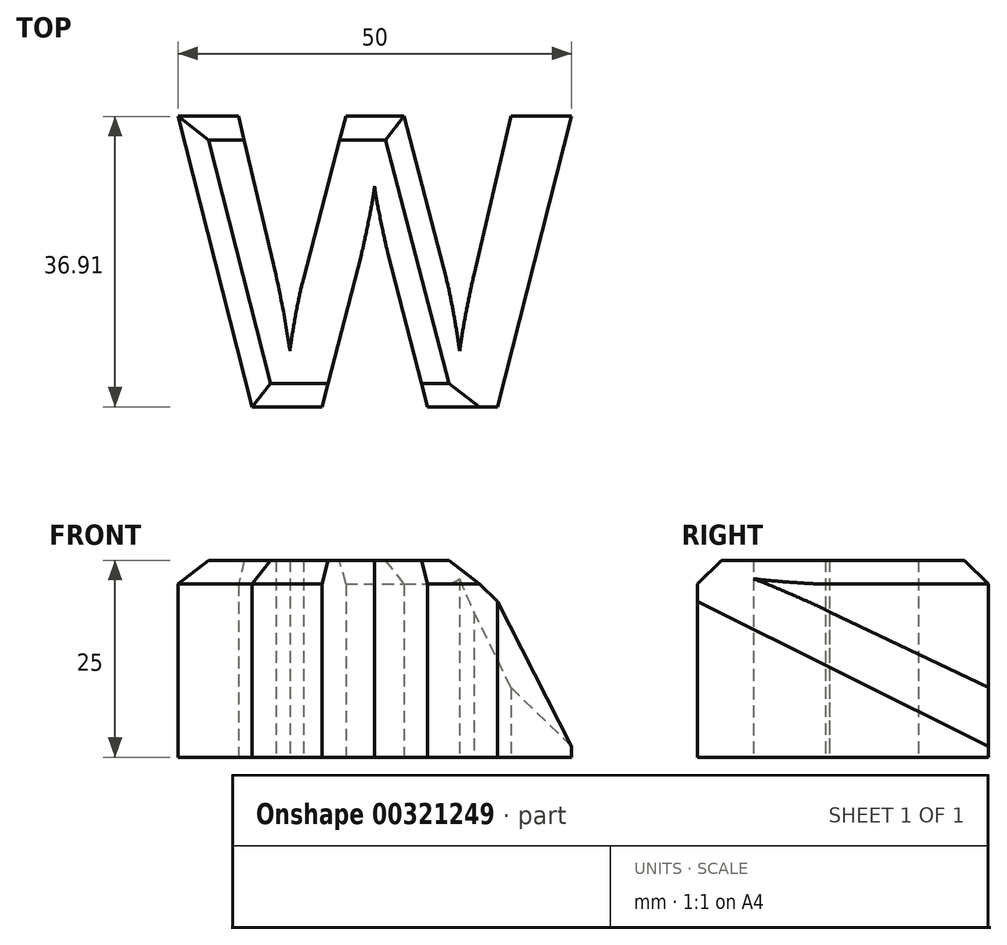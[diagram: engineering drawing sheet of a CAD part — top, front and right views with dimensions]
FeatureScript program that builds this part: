
annotation { "Feature Type Name" : "Feature", "Feature Type Description" : "" }
export const myFeature = defineFeature(function(context is Context, id is Id, definition is map)
    precondition{}
    {
        {
            var Q0;
            Q0=qCreatedBy(makeId("Top.planeOp"),FACE);
            var sketch = newSketch(context, id + "F0", { "sketchPlane" : qUnion([Q0])});
            skText(sketch, "E0", { "text": "W", "fontName": "OpenSans-Bold.ttf"});
            const initialGuessF0  = {"E0": [-0.04309, 0.0045, 1, 0, 0.03723]};
            skSetInitialGuess(sketch, initialGuessF0);
            skSolve(sketch);
        }
        {
            var Q0;
            Q0 = qSketchRegion(id + "F0", true);
            extrude(context, id + "F1", {"entities" : qUnion([Q0]), "depth" : 25 * mm});
        }
        {
            var Q0;
            Q0=makeQuery(id+"F1.opExtrude","CAP_EDGE",EDGE,{"disambiguationData":[OSD([sQuery(id+"F0.wireOp",EDGE,"E0.sketch_text.stroke-8")])],"isStart":false});
            var Q1;
            Q1=makeQuery(id+"F1.opExtrude","CAP_EDGE",EDGE,{"disambiguationData":[OSD([sQuery(id+"F0.wireOp",EDGE,"E0.sketch_text.stroke-9")])],"isStart":false});
            var Q2;
            Q2=makeQuery(id+"F1.opExtrude","CAP_EDGE",EDGE,{"disambiguationData":[OSD([sQuery(id+"F0.wireOp",EDGE,"E0.sketch_text.stroke-7")])],"isStart":false});
            var Q3;
            Q3=makeQuery(id+"F1.opExtrude","CAP_EDGE",EDGE,{"disambiguationData":[OSD([sQuery(id+"F0.wireOp",EDGE,"E0.sketch_text.stroke-23")])],"isStart":false});
            var Q4;
            Q4=makeQuery(id+"F1.opExtrude","CAP_EDGE",EDGE,{"disambiguationData":[OSD([sQuery(id+"F0.wireOp",EDGE,"E0.sketch_text.stroke-0")])],"isStart":false});
            var Q5;
            Q5=makeQuery(id+"F1.opExtrude","CAP_EDGE",EDGE,{"disambiguationData":[OSD([sQuery(id+"F0.wireOp",EDGE,"E0.sketch_text.stroke-22")])],"isStart":false});
            var Q6;
            Q6=makeQuery(id+"F1.opExtrude","CAP_EDGE",EDGE,{"disambiguationData":[OSD([sQuery(id+"F0.wireOp",EDGE,"E0.sketch_text.stroke-15")])],"isStart":false});
            var Q7;
            Q7=makeQuery(id+"F1.opExtrude","CAP_EDGE",EDGE,{"disambiguationData":[OSD([sQuery(id+"F0.wireOp",EDGE,"E0.sketch_text.stroke-16")])],"isStart":false});
            chamfer(context, id + "F2", {"entities" : qUnion([Q0, Q1, Q2, Q3, Q4, Q5, Q6, Q7]), "width" : 3 * mm, "tangentPropagation" : true});
        }
    });
